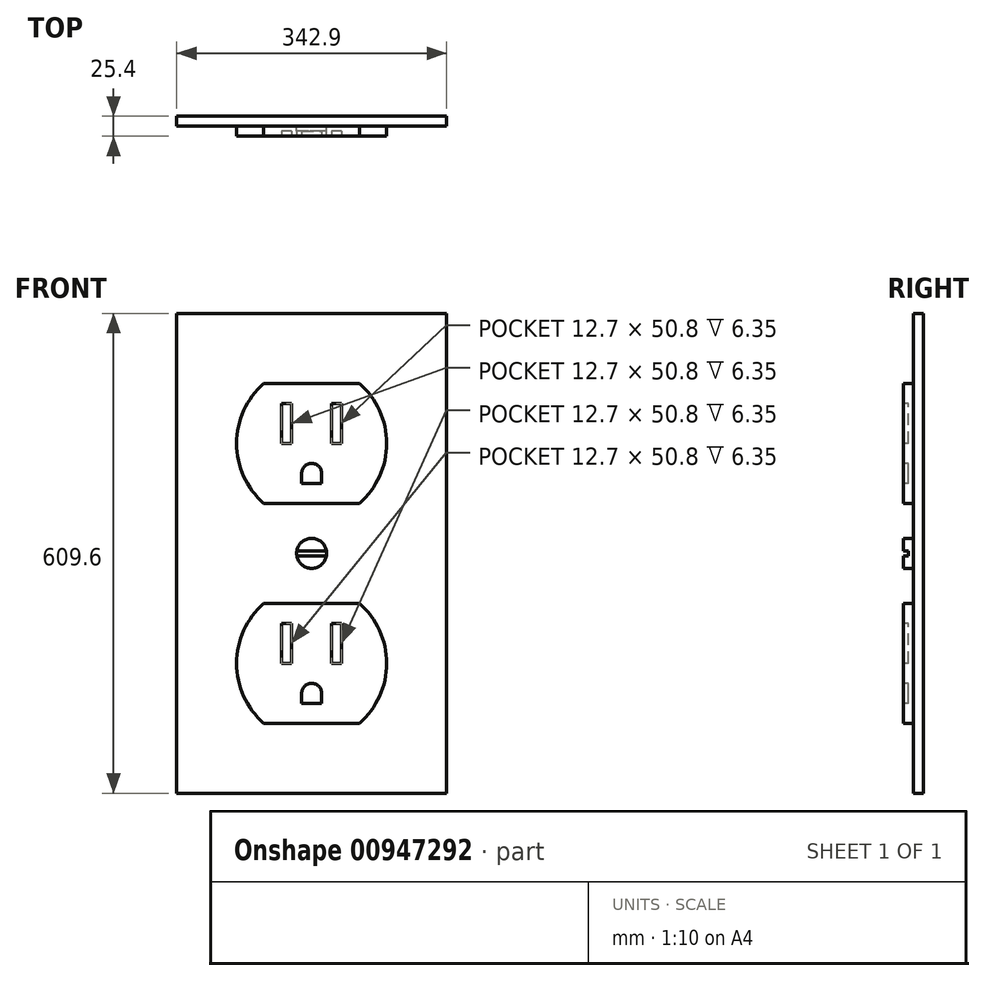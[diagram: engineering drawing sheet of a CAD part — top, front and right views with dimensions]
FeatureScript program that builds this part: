
annotation { "Feature Type Name" : "Feature", "Feature Type Description" : "" }
export const myFeature = defineFeature(function(context is Context, id is Id, definition is map)
    precondition{}
    {
        {
            var Q0;
            Q0=qCreatedBy(makeId("Front.planeOp"),FACE);
            var sketch = newSketch(context, id + "F0", { "sketchPlane" : qUnion([Q0])});
            skLineSegment(sketch, "E0.bottom", {"start": v(171.45, 304.8) * mm, "end": v(-171.45, 304.8) * mm});
            skLineSegment(sketch, "E0.top", {"start": v(171.45, -304.8) * mm, "end": v(-171.45, -304.8) * mm});
            skLineSegment(sketch, "E0.left", {"start": v(171.45, 304.8) * mm, "end": v(171.45, -304.8) * mm});
            skLineSegment(sketch, "E0.right", {"start": v(-171.45, 304.8) * mm, "end": v(-171.45, -304.8) * mm});
            skPoint(sketch, "E0.middle", {"position": v(0, 0) * mm});
            skSolve(sketch);
        }
        {
            var Q0;
            Q0=makeQuery(id+"F0.imprint","IMPRINT",FACE,{"disambiguationData":[TD([[makeQuery(id+"F0.imprint","IMPRINT",EDGE,{"derivedFrom":sQuery(id+"F0.wireOp",EDGE,"E0.bottom")}),1.0]])]});
            extrude(context, id + "F1", {"entities" : qUnion([Q0]), "endBound" : BoundingType.SYMMETRIC, "depth" : 12.7 * mm, "offsetDistance" : 25.4 * mm});
        }
        {
            var Q0;
            Q0=makeQuery(id+"F1.opExtrude","CAP_FACE",FACE,{"disambiguationData":[OSD([sQuery(id+"F0.wireOp",EDGE,"E0.bottom"),sQuery(id+"F0.wireOp",EDGE,"E0.top"),sQuery(id+"F0.wireOp",EDGE,"E0.left"),sQuery(id+"F0.wireOp",EDGE,"E0.right")])],"isStart":false});
            var sketch = newSketch(context, id + "F2", { "sketchPlane" : qUnion([Q0])});
            skLineSegment(sketch, "E1", {"start": v(-60.85, 215.9) * mm, "end": v(60.85, 215.9) * mm});
            skLineSegment(sketch, "E2", {"start": v(-60.85, 63.5) * mm, "end": v(60.85, 63.5) * mm});
            skLineSegment(sketch, "E3", {"start": v(-60.85, -63.5) * mm, "end": v(60.85, -63.5) * mm});
            skLineSegment(sketch, "E4", {"start": v(-60.85, -215.9) * mm, "end": v(60.85, -215.9) * mm});
            skCircle(sketch, "E5", {"center": v(0, 0) * mm, "radius": 19.05 * mm});
            skArc(sketch, "E6", {"start": v(-60.85, 215.9) * mm, "mid": v(-95.25, 139.7) * mm, "end": v(-60.85, 63.5) * mm});
            skArc(sketch, "E7", {"start": v(60.85, 63.5) * mm, "mid": v(95.25, 139.7) * mm, "end": v(60.85, 215.9) * mm});
            skArc(sketch, "E8", {"start": v(60.85, -215.9) * mm, "mid": v(95.25, -139.7) * mm, "end": v(60.85, -63.5) * mm});
            skArc(sketch, "E9", {"start": v(-60.85, -63.5) * mm, "mid": v(-95.25, -139.7) * mm, "end": v(-60.85, -215.9) * mm});
            skSolve(sketch);
        }
        {
            var Q0;
            Q0 = qSketchRegion(id + "F2", true);
            extrude(context, id + "F3", {"entities" : qUnion([Q0]), "depth" : 12.7 * mm, "offsetDistance" : 25.4 * mm});
        }
        {
            var Q0;
            Q0=makeQuery(id+"F3.opExtrude","CAP_FACE",FACE,{"disambiguationData":[OSD([sQuery(id+"F2.wireOp",EDGE,"E1"),sQuery(id+"F2.wireOp",EDGE,"E2"),sQuery(id+"F2.wireOp",EDGE,"E6"),sQuery(id+"F2.wireOp",EDGE,"E7")])],"isStart":false});
            var sketch = newSketch(context, id + "F4", { "sketchPlane" : qUnion([Q0])});
            skLineSegment(sketch, "E10.bottom", {"start": v(-25.4, 139.7) * mm, "end": v(-38.1, 139.7) * mm});
            skLineSegment(sketch, "E10.top", {"start": v(-25.4, 190.5) * mm, "end": v(-38.1, 190.5) * mm});
            skLineSegment(sketch, "E10.left", {"start": v(-25.4, 139.7) * mm, "end": v(-25.4, 190.5) * mm});
            skLineSegment(sketch, "E10.right", {"start": v(-38.1, 139.7) * mm, "end": v(-38.1, 190.5) * mm});
            skPoint(sketch, "E10.middle", {"position": v(-31.75, 165.1) * mm});
            skLineSegment(sketch, "E11.bottom", {"start": v(38.1, 139.7) * mm, "end": v(25.4, 139.7) * mm});
            skLineSegment(sketch, "E11.top", {"start": v(38.1, 190.5) * mm, "end": v(25.4, 190.5) * mm});
            skLineSegment(sketch, "E11.left", {"start": v(38.1, 139.7) * mm, "end": v(38.1, 190.5) * mm});
            skLineSegment(sketch, "E11.right", {"start": v(25.4, 139.7) * mm, "end": v(25.4, 190.5) * mm});
            skPoint(sketch, "E11.middle", {"position": v(31.75, 165.1) * mm});
            skLineSegment(sketch, "E12.bottom", {"start": v(-25.4, -139.7) * mm, "end": v(-38.1, -139.7) * mm});
            skLineSegment(sketch, "E12.top", {"start": v(-25.4, -88.9) * mm, "end": v(-38.1, -88.9) * mm});
            skLineSegment(sketch, "E12.left", {"start": v(-25.4, -139.7) * mm, "end": v(-25.4, -88.9) * mm});
            skLineSegment(sketch, "E12.right", {"start": v(-38.1, -139.7) * mm, "end": v(-38.1, -88.9) * mm});
            skPoint(sketch, "E12.middle", {"position": v(-31.75, -114.3) * mm});
            skLineSegment(sketch, "E13.bottom", {"start": v(38.1, -139.7) * mm, "end": v(25.4, -139.7) * mm});
            skLineSegment(sketch, "E13.top", {"start": v(38.1, -88.9) * mm, "end": v(25.4, -88.9) * mm});
            skLineSegment(sketch, "E13.left", {"start": v(38.1, -139.7) * mm, "end": v(38.1, -88.9) * mm});
            skLineSegment(sketch, "E13.right", {"start": v(25.4, -139.7) * mm, "end": v(25.4, -88.9) * mm});
            skPoint(sketch, "E13.middle", {"position": v(31.75, -114.3) * mm});
            skLineSegment(sketch, "E14.bottom", {"start": v(55.14, 3.18) * mm, "end": v(-55.14, 3.18) * mm});
            skLineSegment(sketch, "E14.top", {"start": v(55.14, -3.17) * mm, "end": v(-55.14, -3.17) * mm});
            skLineSegment(sketch, "E14.left", {"start": v(55.14, 3.18) * mm, "end": v(55.14, -3.17) * mm});
            skLineSegment(sketch, "E14.right", {"start": v(-55.14, 3.18) * mm, "end": v(-55.14, -3.17) * mm});
            skPoint(sketch, "E14.middle", {"position": v(0, 0) * mm});
            skLineSegment(sketch, "E15", {"start": v(-12.7, 88.9) * mm, "end": v(-12.7, 88.9) * mm});
            skLineSegment(sketch, "E16", {"start": v(-12.7, 88.9) * mm, "end": v(12.7, 88.9) * mm});
            skLineSegment(sketch, "E17", {"start": v(12.7, 88.9) * mm, "end": v(12.7, 101.6) * mm});
            skLineSegment(sketch, "E18", {"start": v(-12.7, -190.5) * mm, "end": v(-12.7, -190.5) * mm});
            skLineSegment(sketch, "E19", {"start": v(-12.7, -190.5) * mm, "end": v(12.7, -190.5) * mm});
            skLineSegment(sketch, "E20", {"start": v(12.7, -190.5) * mm, "end": v(12.7, -177.8) * mm});
            skLineSegment(sketch, "E21", {"start": v(-12.7, 88.9) * mm, "end": v(-12.7, 101.6) * mm});
            skArc(sketch, "E22", {"start": v(12.7, 101.6) * mm, "mid": v(0, 114.3) * mm, "end": v(-12.7, 101.6) * mm});
            skLineSegment(sketch, "E23", {"start": v(-12.7, -190.5) * mm, "end": v(-12.7, -177.8) * mm});
            skArc(sketch, "E24", {"start": v(12.7, -177.8) * mm, "mid": v(0, -165.1) * mm, "end": v(-12.7, -177.8) * mm});
            skSolve(sketch);
        }
        {
            var Q0;
            Q0 = qSketchRegion(id + "F4", true);
            extrude(context, id + "F5", {"entities" : qUnion([Q0]), "operationType" : NewBodyOperationType.REMOVE, "oppositeDirection" : true, "depth" : 6.35 * mm, "offsetDistance" : 25.4 * mm});
        }
        {
            var Q0;
            Q0=makeQuery(id+"F3.opExtrude","SWEPT_BODY",BODY,{"disambiguationData":[OSD([sQuery(id+"F2.wireOp",EDGE,"E1"),sQuery(id+"F2.wireOp",EDGE,"E2"),sQuery(id+"F2.wireOp",EDGE,"E6"),sQuery(id+"F2.wireOp",EDGE,"E7")])]});
            var Q1;
            Q1=makeQuery(id+"F3.opExtrude","SWEPT_BODY",BODY,{"disambiguationData":[OSD([sQuery(id+"F2.wireOp",EDGE,"E3"),sQuery(id+"F2.wireOp",EDGE,"E4"),sQuery(id+"F2.wireOp",EDGE,"E8"),sQuery(id+"F2.wireOp",EDGE,"E9")])]});
            var Q2;
            Q2=makeQuery(id+"F1.opExtrude","SWEPT_BODY",BODY,{"disambiguationData":[OSD([sQuery(id+"F0.wireOp",EDGE,"E0.bottom"),sQuery(id+"F0.wireOp",EDGE,"E0.top"),sQuery(id+"F0.wireOp",EDGE,"E0.left"),sQuery(id+"F0.wireOp",EDGE,"E0.right")])]});
            var Q3;
            Q3=makeQuery(id+"F3.opExtrude","SWEPT_BODY",BODY,{"disambiguationData":[OSD([sQuery(id+"F2.wireOp",EDGE,"E5")])]});
            var Q4;
            Q4=qCreatedBy(makeId("Origin.pointOp"),VERTEX);
            transform(context, id + "F6", {"entities" : qUnion([Q0, Q1, Q2, Q3]), "transformType" : TransformType.SCALE_UNIFORMLY, "scale" : 1, "scalePoint" : qUnion([Q4]), "makeCopy" : false});
        }
    });
